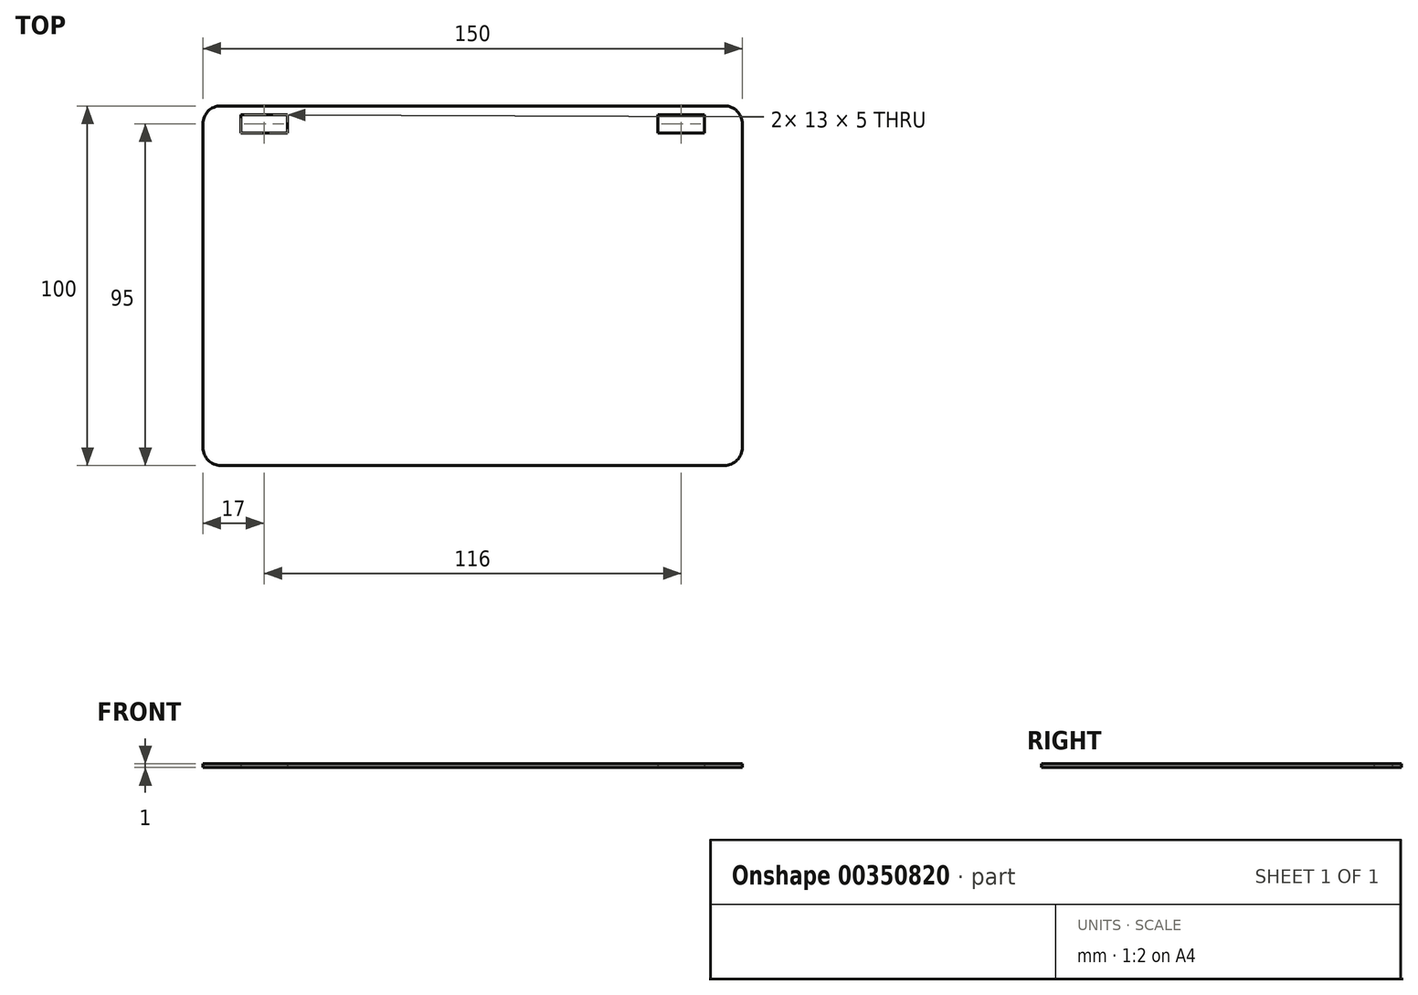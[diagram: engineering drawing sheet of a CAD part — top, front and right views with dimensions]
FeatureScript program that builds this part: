
annotation { "Feature Type Name" : "Feature", "Feature Type Description" : "" }
export const myFeature = defineFeature(function(context is Context, id is Id, definition is map)
    precondition{}
    {
        {
            var Q0;
            Q0=qCreatedBy(makeId("Top.planeOp"),FACE);
            var sketch = newSketch(context, id + "F0", { "sketchPlane" : qUnion([Q0])});
            skLineSegment(sketch, "E0.bottom", {"start": v(70, -50) * mm, "end": v(-70, -50) * mm});
            skLineSegment(sketch, "E0.top", {"start": v(70, 50) * mm, "end": v(-70, 50) * mm});
            skLineSegment(sketch, "E0.left", {"start": v(75, -45) * mm, "end": v(75, 45) * mm});
            skLineSegment(sketch, "E0.right", {"start": v(-75, -45) * mm, "end": v(-75, 45) * mm});
            skPoint(sketch, "E0.middle", {"position": v(0, 0) * mm});
            skPoint(sketch, "E1.visualSharp", {"position": v(-75, 50) * mm});
            skArc(sketch, "E1.filletArc", {"start": v(-70, 50) * mm, "mid": v(-73.54, 48.54) * mm, "end": v(-75, 45) * mm});
            skPoint(sketch, "E2.visualSharp", {"position": v(75, 50) * mm});
            skArc(sketch, "E2.filletArc", {"start": v(75, 45) * mm, "mid": v(73.54, 48.54) * mm, "end": v(70, 50) * mm});
            skPoint(sketch, "E3.visualSharp", {"position": v(75, -50) * mm});
            skArc(sketch, "E3.filletArc", {"start": v(70, -50) * mm, "mid": v(73.54, -48.54) * mm, "end": v(75, -45) * mm});
            skPoint(sketch, "E4.visualSharp", {"position": v(-75, -50) * mm});
            skArc(sketch, "E4.filletArc", {"start": v(-75, -45) * mm, "mid": v(-73.54, -48.54) * mm, "end": v(-70, -50) * mm});
            skLineSegment(sketch, "E5.bottom", {"start": v(-64.5, 47.5) * mm, "end": v(-51.5, 47.5) * mm});
            skLineSegment(sketch, "E5.top", {"start": v(-64.5, 42.5) * mm, "end": v(-51.5, 42.5) * mm});
            skLineSegment(sketch, "E5.left", {"start": v(-64.5, 47.5) * mm, "end": v(-64.5, 42.5) * mm});
            skLineSegment(sketch, "E5.right", {"start": v(-51.5, 47.5) * mm, "end": v(-51.5, 42.5) * mm});
            skLineSegment(sketch, "E6", {"start": v(-58, 47.5) * mm, "end": v(-58, 42.5) * mm, "construction": true});
            skLineSegment(sketch, "E7", {"start": v(-64.5, 45) * mm, "end": v(-51.5, 45) * mm, "construction": true});
            skLineSegment(sketch, "E8", {"start": v(0, -3.14) * mm, "end": v(0, 4.19) * mm, "construction": true});
            skLineSegment(sketch, "E9", {"start": v(8.24, 0) * mm, "end": v(-6.15, 0) * mm, "construction": true});
            skLineSegment(sketch, "E10.MirrorCS", {"start": v(64.5, 47.5) * mm, "end": v(51.5, 47.5) * mm});
            skLineSegment(sketch, "E11.MirrorCS", {"start": v(58, 47.5) * mm, "end": v(58, 42.5) * mm, "construction": true});
            skLineSegment(sketch, "E12.MirrorCS", {"start": v(64.5, 45) * mm, "end": v(51.5, 45) * mm, "construction": true});
            skLineSegment(sketch, "E13.MirrorCS", {"start": v(51.5, 47.5) * mm, "end": v(51.5, 42.5) * mm});
            skLineSegment(sketch, "E14.MirrorCS", {"start": v(64.5, 47.5) * mm, "end": v(64.5, 42.5) * mm});
            skLineSegment(sketch, "E15.MirrorCS", {"start": v(64.5, 42.5) * mm, "end": v(51.5, 42.5) * mm});
            skSolve(sketch);
        }
        {
            var Q0;
            Q0 = qSketchRegion(id + "F0", true);
            extrude(context, id + "F1", {"entities" : qUnion([Q0]), "depth" : 1 * mm});
        }
    });
